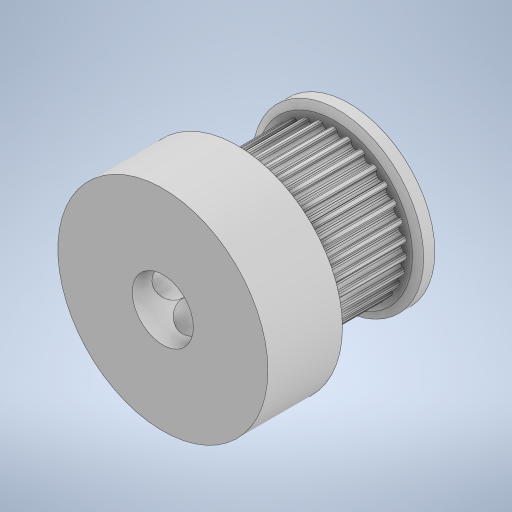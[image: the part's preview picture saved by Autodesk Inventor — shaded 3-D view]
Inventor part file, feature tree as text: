
AUTODESK INVENTOR PART (.ipt)
format: ipt  version: 2024 (Build 280153000, 153)  size: 1,526,784 bytes
history: native  units: mm
features: extrude x5, sketch x5, plane x4, projected_geometry x2, pattern_circular x1, chamfer x1, mirror x1, direct_edit x1, move_body x1
ambient origin geometry x8: Origin, YZ Plane, XZ Plane, XY Plane, X Axis, Y Axis, Z Axis, Center Point
bodies: Solid1 (feature_tree)
feature tree (21):
  extrude  "Extrusion1"  Depth=1.0mm
  pattern_circular  "Circular Pattern1"  [2 undecoded]
  extrude  "Extrusion2"  Depth=14.1mm
  chamfer  "Chamfer1"  Distance=0.6mm
  mirror  "Mirror1"
  extrude  "Extrusion8"  Depth=14.1mm
  sketch  "Sketch14"  dims[d3=1.004mm]
  plane  "Work Plane8"
  plane  "Work Plane9"
  plane  "Work Plane10"
  plane  "Work Plane11"
  extrude  "Extrusion10"  TaperAngle=0.0deg  [1 undecoded]
  extrude  "Extrusion11"  Depth=14.1mm
  direct_edit  "Direct Edit1"
  sketch  "Sketch1"  dims[d0=20.0mm d1=1.0mm]
  sketch  "Sketch12"  dims[d2=0.4mm]
  projected_geometry  "Projected Loop6"
  sketch  "Sketch15"  dims[d4=0.75mm]
  projected_geometry  "Projected Loop8"
  sketch  "Sketch16"  dims[d5=0.555mm d6=1.0mm d7=0.15mm d9=0.6mm d10=11.0mm d11=0.0mm d12=314.159265mm d13=360.0deg d15=23.0mm d16=2.0mm d17=0.0mm d18=1.0mm d19=0.5mm d20=45.0deg d21=8.2mm d42=10.0mm d43=9.0mm d44=0.0mm d49=90.0deg d50=90.0deg d51=5.75mm d52=4.5mm d55=9.0mm d56=0.0mm d57=5.8mm d58=10.0mm d59=0.0mm d61=14.1mm d62=0.0mm d63=0.0mm d64=1.0mm]
  move_body  "Move1"
note: 3 required parameter values undecoded (feature->parameter linkage not recoverable at this tier; creation-order binding heuristic only, values carry confidence <= 0.55)
